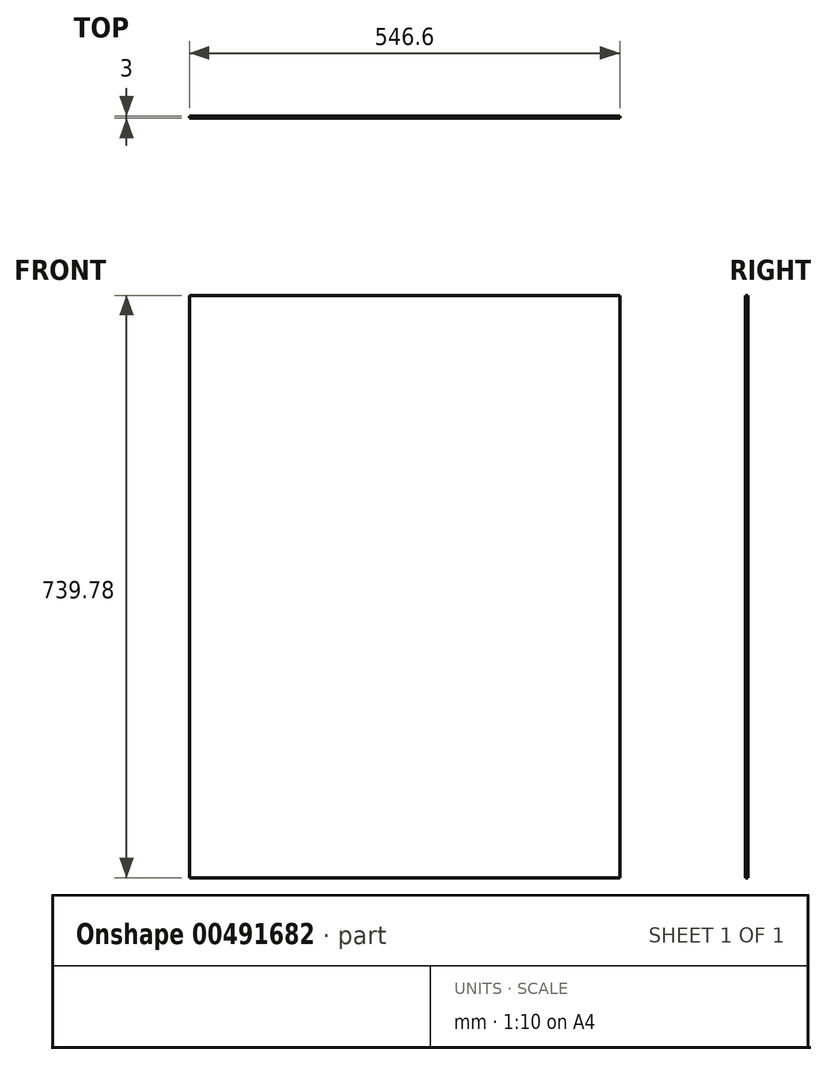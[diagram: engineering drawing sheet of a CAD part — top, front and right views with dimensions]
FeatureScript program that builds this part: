
annotation { "Feature Type Name" : "Feature", "Feature Type Description" : "" }
export const myFeature = defineFeature(function(context is Context, id is Id, definition is map)
    precondition{}
    {
        {
            var Q0;
            Q0=qCreatedBy(makeId("Front.planeOp"),FACE);
            var sketch = newSketch(context, id + "F0", { "sketchPlane" : qUnion([Q0])});
            skLineSegment(sketch, "E0.bottom", {"start": v(-277.11, 452.58) * mm, "end": v(269.5, 452.58) * mm});
            skLineSegment(sketch, "E0.top", {"start": v(-277.11, -287.2) * mm, "end": v(269.5, -287.2) * mm});
            skLineSegment(sketch, "E0.left", {"start": v(-277.11, 452.58) * mm, "end": v(-277.11, -287.2) * mm});
            skLineSegment(sketch, "E0.right", {"start": v(269.5, 452.58) * mm, "end": v(269.5, -287.2) * mm});
            skSolve(sketch);
        }
        {
            var Q0;
            Q0 = qSketchRegion(id + "F0", true);
            extrude(context, id + "F1", {"entities" : qUnion([Q0]), "depth" : 3 * mm});
        }
    });
